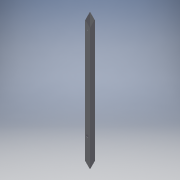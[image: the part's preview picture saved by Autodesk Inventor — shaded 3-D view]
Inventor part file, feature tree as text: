
AUTODESK INVENTOR PART (.ipt)
format: ipt  version: 2016 (Build 200138000, 138)  size: 131,584 bytes
history: native  units: in
note: dims shown in document units (in); Inventor stores cm internally (conversion verified against a paired STEP export)
features: extrude x5, sketch x5
ambient origin geometry x8: Origin, YZ Plane, XZ Plane, XY Plane, X Axis, Y Axis, Z Axis, Center Point
bodies: Solid1 (feature_tree)
feature tree (10):
  extrude  "Extrusion1"  Depth=1.0in
  extrude  "Extrusion2"  Depth=27.5in TaperAngle=0.0deg
  extrude  "Extrusion7"  Depth=0.5in
  extrude  "Extrusion11"  Depth=1.0in
  extrude  "Extrusion12"  Depth=1.0in TaperAngle=0.0deg
  sketch  "Sketch1"  dims[d0=1.0in d1=1.0in]
  sketch  "Sketch2"  dims[d2=0.0625in d3=27.5in d4=0.0in]
  sketch  "Sketch7"  dims[d5=0.5in d6=0.5in]
  sketch  "Sketch11"  dims[d7=1.0in d8=0.0in d26=0.5in]
  sketch  "Sketch12"  dims[d27=5.98in d28=1.0in d29=0.0in d31=0.45in d43=1.0in d44=0.0in d46=0.25in d47=1.0in d48=0.25in d50=3.0in d51=0.0625in d52=0.0in]
